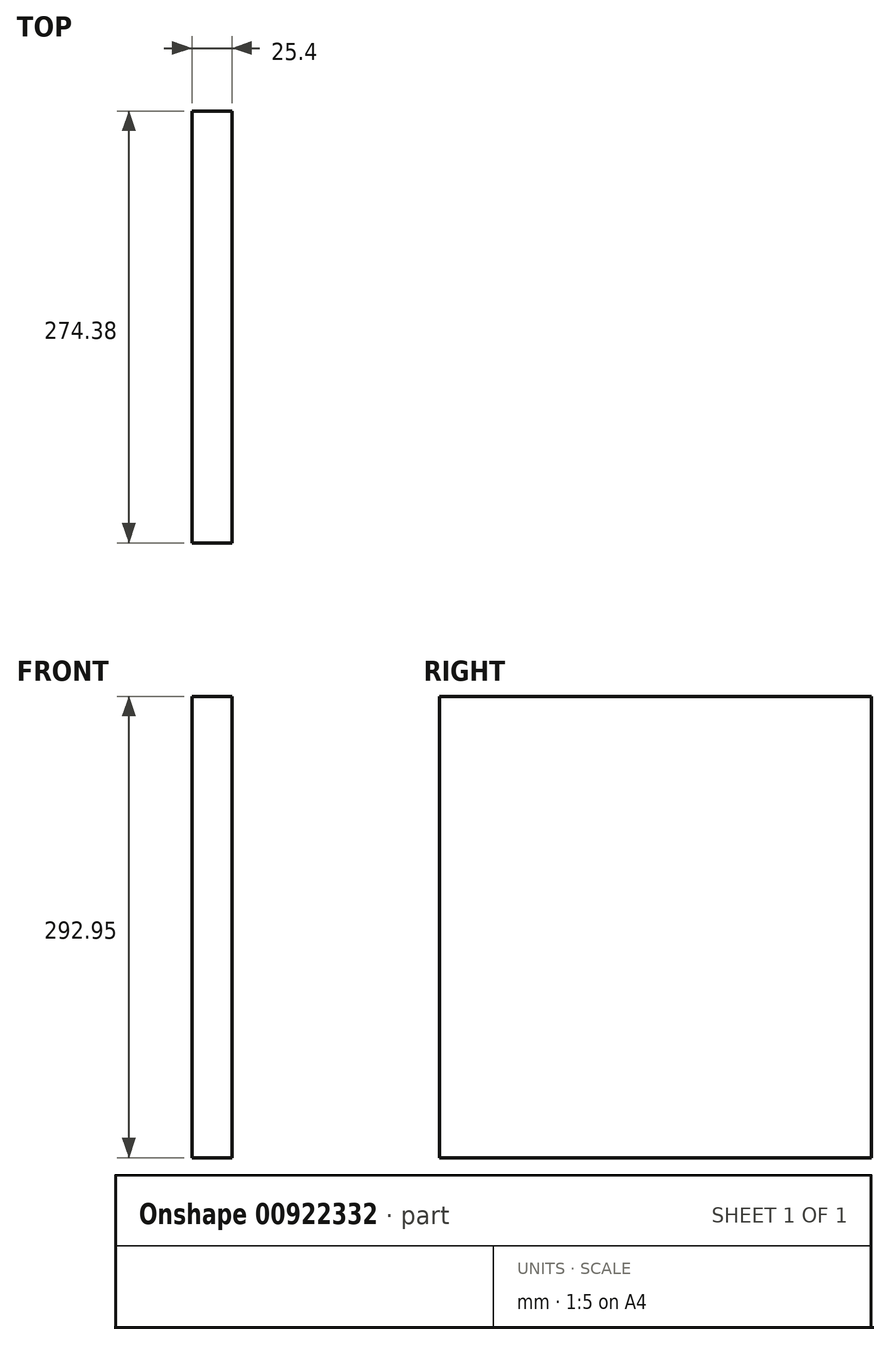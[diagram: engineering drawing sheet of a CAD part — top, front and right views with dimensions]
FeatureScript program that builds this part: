
annotation { "Feature Type Name" : "Feature", "Feature Type Description" : "" }
export const myFeature = defineFeature(function(context is Context, id is Id, definition is map)
    precondition{}
    {
        {
            var Q0;
            Q0=qCreatedBy(makeId("Right.planeOp"),FACE);
            var sketch = newSketch(context, id + "F0", { "sketchPlane" : qUnion([Q0])});
            skLineSegment(sketch, "E0.bottom", {"start": v(0, 0) * mm, "end": v(-274.38, 0) * mm});
            skLineSegment(sketch, "E0.top", {"start": v(0, 292.95) * mm, "end": v(-274.38, 292.95) * mm});
            skLineSegment(sketch, "E0.left", {"start": v(0, 0) * mm, "end": v(0, 292.95) * mm});
            skLineSegment(sketch, "E0.right", {"start": v(-274.38, 0) * mm, "end": v(-274.38, 292.95) * mm});
            skSolve(sketch);
        }
        {
            var Q0;
            Q0=makeQuery(id+"F0.imprint","IMPRINT",FACE,{"disambiguationData":[TD([[makeQuery(id+"F0.imprint","IMPRINT",EDGE,{"derivedFrom":sQuery(id+"F0.wireOp",EDGE,"E0.bottom")}),-1.0]])]});
            extrude(context, id + "F1", {"entities" : qUnion([Q0]), "depth" : 25.4 * mm, "offsetDistance" : 25.4 * mm});
        }
    });
